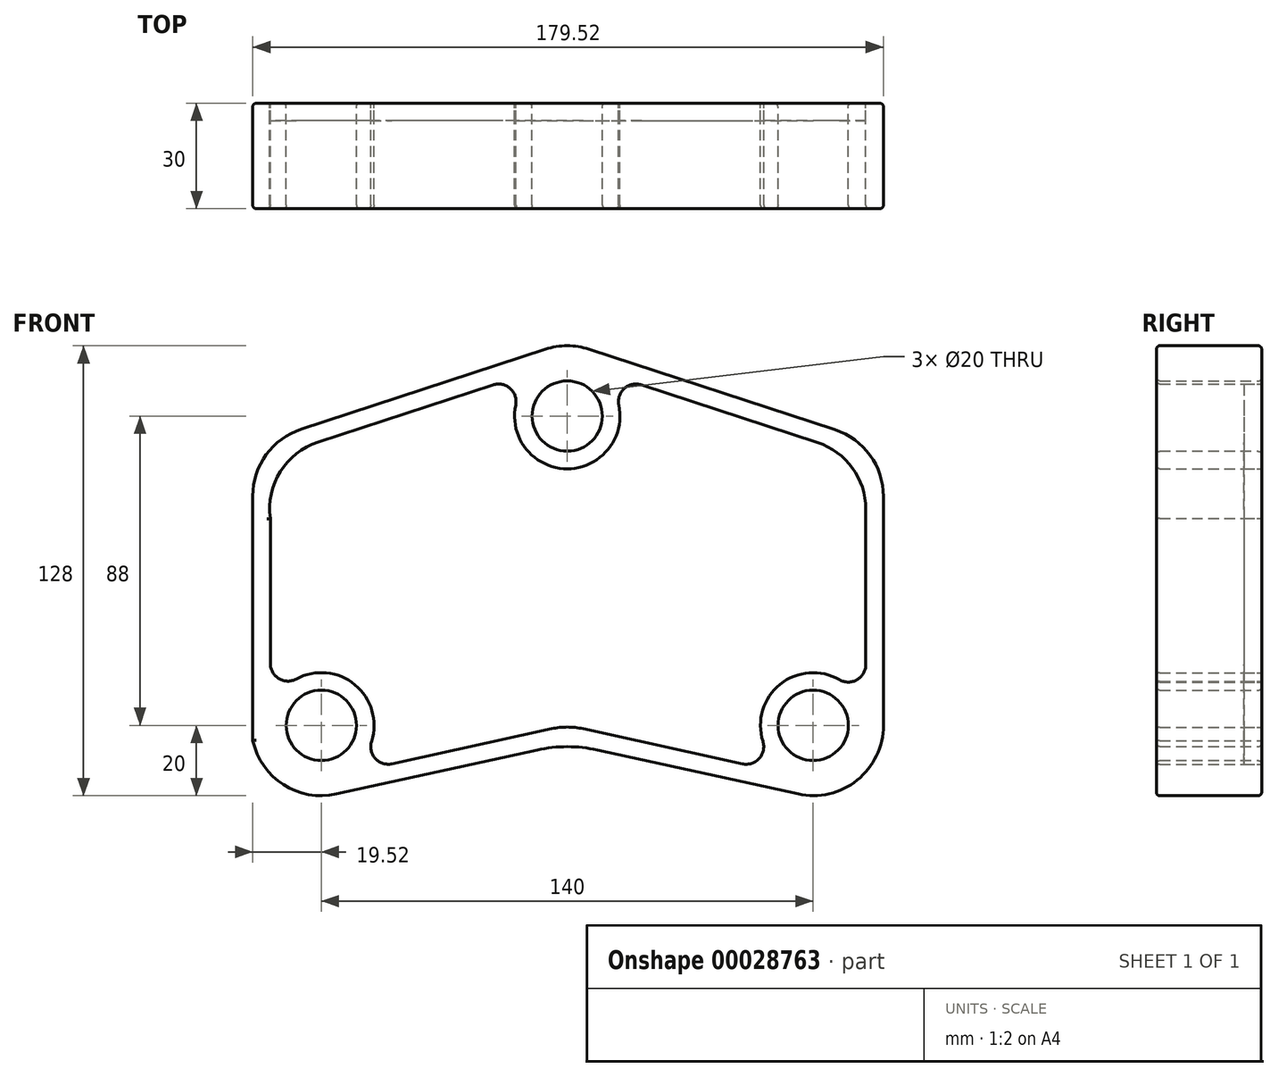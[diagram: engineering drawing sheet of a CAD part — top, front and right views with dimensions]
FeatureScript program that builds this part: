
annotation { "Feature Type Name" : "Feature", "Feature Type Description" : "" }
export const myFeature = defineFeature(function(context is Context, id is Id, definition is map)
    precondition{}
    {
        {
            var Q0;
            Q0=qCreatedBy(makeId("Front.planeOp"),FACE);
            var sketch = newSketch(context, id + "F0", { "sketchPlane" : qUnion([Q0])});
            skCircle(sketch, "E0", {"center": v(0, 0) * mm, "radius": 10 * mm});
            skLineSegment(sketch, "E1", {"start": v(-6.22, 19) * mm, "end": v(-75.74, -3.73) * mm});
            skLineSegment(sketch, "E2", {"start": v(-89.52, -22.74) * mm, "end": v(-89.52, -92.34) * mm});
            skLineSegment(sketch, "E3", {"start": v(6.22, 19) * mm, "end": v(76.22, -3.89) * mm});
            skLineSegment(sketch, "E4", {"start": v(90, -88) * mm, "end": v(90, -22.9) * mm});
            skLineSegment(sketch, "E5", {"start": v(-21.13, 8.87) * mm, "end": v(-70.93, -7.42) * mm});
            skCircle(sketch, "E6", {"center": v(-70, -88) * mm, "radius": 10 * mm});
            skCircle(sketch, "E7", {"center": v(70, -88) * mm, "radius": 10 * mm});
            skLineSegment(sketch, "E8", {"start": v(21.13, 8.87) * mm, "end": v(71.22, -7.51) * mm});
            skLineSegment(sketch, "E9", {"start": v(0, 0) * mm, "end": v(0, -109.62) * mm, "construction": true});
            skLineSegment(sketch, "E10", {"start": v(85, -26.52) * mm, "end": v(85, -70.68) * mm});
            skPoint(sketch, "E11.visualSharp", {"position": v(-89.52, -8.24) * mm});
            skArc(sketch, "E11.filletArc", {"start": v(-75.74, -3.73) * mm, "mid": v(-85.72, -11) * mm, "end": v(-89.52, -22.74) * mm});
            skPoint(sketch, "E12.visualSharp", {"position": v(90, -8.4) * mm});
            skArc(sketch, "E12.filletArc", {"start": v(90, -22.9) * mm, "mid": v(86.2, -11.16) * mm, "end": v(76.22, -3.89) * mm});
            skPoint(sketch, "E13.visualSharp", {"position": v(-86.08, -12.37) * mm});
            skArc(sketch, "E13.filletArc", {"start": v(-70.93, -7.42) * mm, "mid": v(-81.67, -15.83) * mm, "end": v(-84.52, -29.17) * mm});
            skPoint(sketch, "E14.visualSharp", {"position": v(85, -12.02) * mm});
            skArc(sketch, "E14.filletArc", {"start": v(85, -26.52) * mm, "mid": v(81.2, -14.78) * mm, "end": v(71.22, -7.51) * mm});
            skPoint(sketch, "E15.visualSharp", {"position": v(0, 21.04) * mm});
            skArc(sketch, "E15.filletArc", {"start": v(6.22, 19) * mm, "mid": v(0, 20) * mm, "end": v(-6.22, 19) * mm});
            skArc(sketch, "E16.filletArc", {"start": v(4.5, -88.97) * mm, "mid": v(0.02, -88.49) * mm, "end": v(-4.45, -88.98) * mm});
            skLineSegment(sketch, "E17.0", {"start": v(-65.71, -107.54) * mm, "end": v(-8.58, -95) * mm});
            skLineSegment(sketch, "E18.0", {"start": v(8.58, -95) * mm, "end": v(65.71, -107.54) * mm});
            skArc(sketch, "E19.filletArc", {"start": v(8.58, -95) * mm, "mid": v(0, -94.06) * mm, "end": v(-8.58, -95) * mm});
            skArc(sketch, "E20", {"start": v(-89.52, -92.34) * mm, "mid": v(-80.76, -104.86) * mm, "end": v(-65.71, -107.54) * mm});
            skArc(sketch, "E21", {"start": v(65.71, -107.54) * mm, "mid": v(82.53, -103.58) * mm, "end": v(90, -88) * mm});
            skArc(sketch, "E22", {"start": v(-55.7, -92.54) * mm, "mid": v(-60.44, -76.44) * mm, "end": v(-77.14, -74.81) * mm});
            skArc(sketch, "E23", {"start": v(66.78, -102.65) * mm, "mid": v(66.78, -102.65) * mm, "end": v(66.78, -102.65) * mm});
            skLineSegment(sketch, "E24", {"start": v(-84.52, -29.17) * mm, "end": v(-84.52, -70.41) * mm});
            skArc(sketch, "E25", {"start": v(-84.52, -70.41) * mm, "mid": v(-82.08, -74.7) * mm, "end": v(-77.14, -74.81) * mm});
            skLineSegment(sketch, "E26", {"start": v(-4.45, -88.98) * mm, "end": v(-49.87, -98.94) * mm});
            skArc(sketch, "E27", {"start": v(-55.7, -92.54) * mm, "mid": v(-54.63, -97.43) * mm, "end": v(-49.87, -98.94) * mm});
            skArc(sketch, "E28", {"start": v(77.5, -75) * mm, "mid": v(82.5, -75) * mm, "end": v(85, -70.68) * mm});
            skLineSegment(sketch, "E29", {"start": v(4.5, -88.97) * mm, "end": v(49.86, -98.94) * mm});
            skArc(sketch, "E30", {"start": v(49.86, -98.94) * mm, "mid": v(54.63, -97.42) * mm, "end": v(55.7, -92.54) * mm});
            skLineSegment(sketch, "E31.trimOffspring", {"start": v(66.78, -102.65) * mm, "end": v(66.78, -102.65) * mm});
            skArc(sketch, "E32.trimOffspring", {"start": v(77.5, -75) * mm, "mid": v(60.6, -76.31) * mm, "end": v(55.7, -92.54) * mm});
            skArc(sketch, "E33", {"start": v(-14.68, 3.09) * mm, "mid": v(0, -15) * mm, "end": v(14.68, 3.09) * mm});
            skArc(sketch, "E34", {"start": v(-14.68, 3.09) * mm, "mid": v(-16.23, 7.84) * mm, "end": v(-21.13, 8.87) * mm});
            skArc(sketch, "E35", {"start": v(21.13, 8.87) * mm, "mid": v(16.23, 7.84) * mm, "end": v(14.68, 3.09) * mm});
            skSolve(sketch);
        }
        {
            var Q0;
            Q0=makeQuery(id+"F0.imprint","IMPRINT",FACE,{"disambiguationData":[TD([[makeQuery(id+"F0.imprint","IMPRINT",EDGE,{"derivedFrom":sQuery(id+"F0.wireOp",EDGE,"E0")}),-1.0]])]});
            extrude(context, id + "F1", {"entities" : qUnion([Q0]), "depth" : 30 * mm});
        }
        {
            var Q0;
            Q0=makeQuery(id+"F0.imprint","IMPRINT",FACE,{"disambiguationData":[TD([[makeQuery(id+"F0.imprint","IMPRINT",EDGE,{"derivedFrom":sQuery(id+"F0.wireOp",EDGE,"E5")}),1.0]])]});
            extrude(context, id + "F2", {"entities" : qUnion([Q0]), "depth" : 5 * mm});
        }
        {
            var Q0;
            Q0=makeQuery(id+"F1.opExtrude","CAP_EDGE",EDGE,{"disambiguationData":[OSD([sQuery(id+"F0.wireOp",EDGE,"E21")])],"isStart":false});
            var Q1;
            Q1=makeQuery(id+"F1.opExtrude","CAP_EDGE",EDGE,{"disambiguationData":[OSD([sQuery(id+"F0.wireOp",EDGE,"E4")])],"isStart":false});
            var Q2;
            Q2=makeQuery(id+"F1.opExtrude","CAP_EDGE",EDGE,{"disambiguationData":[OSD([sQuery(id+"F0.wireOp",EDGE,"E12.filletArc")])],"isStart":false});
            var Q3;
            Q3=makeQuery(id+"F1.opExtrude","CAP_EDGE",EDGE,{"disambiguationData":[OSD([sQuery(id+"F0.wireOp",EDGE,"E26")])],"isStart":false});
            var Q4;
            Q4=makeQuery(id+"F1.opExtrude","CAP_EDGE",EDGE,{"disambiguationData":[OSD([sQuery(id+"F0.wireOp",EDGE,"E29")])],"isStart":false});
            var Q5;
            Q5=makeQuery(id+"F1.opExtrude","CAP_EDGE",EDGE,{"disambiguationData":[OSD([sQuery(id+"F0.wireOp",EDGE,"E16.filletArc")])],"isStart":false});
            var Q6;
            Q6=makeQuery(id+"F1.opExtrude","CAP_EDGE",EDGE,{"disambiguationData":[OSD([sQuery(id+"F0.wireOp",EDGE,"E6")])],"isStart":false});
            var Q7;
            Q7=makeQuery(id+"F1.opExtrude","CAP_EDGE",EDGE,{"disambiguationData":[OSD([sQuery(id+"F0.wireOp",EDGE,"E7")])],"isStart":false});
            var Q8;
            Q8=makeQuery(id+"F1.opExtrude","CAP_EDGE",EDGE,{"disambiguationData":[OSD([sQuery(id+"F0.wireOp",EDGE,"E0")])],"isStart":false});
            var Q9;
            Q9=makeQuery(id+"F1.opExtrude","CAP_EDGE",EDGE,{"disambiguationData":[OSD([sQuery(id+"F0.wireOp",EDGE,"E17.0")])],"isStart":true});
            var Q10;
            Q10=makeQuery(id+"F1.opExtrude","CAP_EDGE",EDGE,{"disambiguationData":[OSD([sQuery(id+"F0.wireOp",EDGE,"E20")])],"isStart":true});
            var Q11;
            Q11=makeQuery(id+"F1.opExtrude","CAP_EDGE",EDGE,{"disambiguationData":[OSD([sQuery(id+"F0.wireOp",EDGE,"E2")])],"isStart":true});
            var Q12;
            Q12=makeQuery(id+"F1.opExtrude","CAP_EDGE",EDGE,{"disambiguationData":[OSD([sQuery(id+"F0.wireOp",EDGE,"E11.filletArc")])],"isStart":true});
            var Q13;
            Q13=makeQuery(id+"F1.opExtrude","CAP_EDGE",EDGE,{"disambiguationData":[OSD([sQuery(id+"F0.wireOp",EDGE,"E0")])],"isStart":true});
            var Q14;
            Q14=makeQuery(id+"F1.opExtrude","CAP_EDGE",EDGE,{"disambiguationData":[OSD([sQuery(id+"F0.wireOp",EDGE,"E6")])],"isStart":true});
            var Q15;
            Q15=makeQuery(id+"F1.opExtrude","CAP_EDGE",EDGE,{"disambiguationData":[OSD([sQuery(id+"F0.wireOp",EDGE,"E7")])],"isStart":true});
            fillet(context, id + "F3", {"entities" : qUnion([Q0, Q1, Q2, Q3, Q4, Q5, Q6, Q7, Q8, Q9, Q10, Q11, Q12, Q13, Q14, Q15]), "radius" : 1 * mm, "tangentPropagation" : true, "allowEdgeOverflow" : false});
        }
    });
